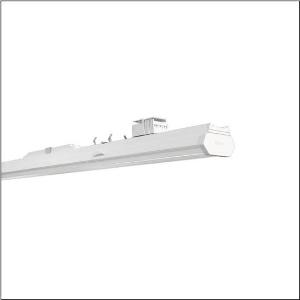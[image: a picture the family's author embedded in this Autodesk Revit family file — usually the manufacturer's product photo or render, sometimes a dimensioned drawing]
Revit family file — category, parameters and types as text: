
# Revit family: licross_r__11_protected_mo_51tp11dn495g_6ace
name_source: partatom
category: Lighting Fixtures
units: mm (PartAtom-declared; Revit-internal decimal feet)

## family parameters
Cut with Voids When Loaded = No
Host = Face
Light Source = No
Part Type = Normal
Room Calculation Point = No
Round Connector Dimension = Use Diameter
Shared = No

## types (1)
- --- (1 x LED, 9930 lm, 57.1 W, 4000K)
    Apparent Load = 57 VA
    CIE Flux Codes = 83 94 98 100 100
    Color Rendering = 80
    Color Temperature = 4000K
    Default Elevation = 1800 mm
    Description = Licross® 11 Protected MO, luminaire insert, of sheet steel, galvanised, coil coated, white, length: 1.500mm, width: 90mm, height: 101mm, LED rated luminous flux: 9.980lm, light colour: 840, SDCM (Standard Deviation of Colour Matching)MacAdam ≤ 2 SDCM (initial), control gear: DALI 2, with plug, 5-pole, with phase selection, mains connection: 220..240V, AC, 50/60Hz, rated input power: 57W, internal wiring halogen-free, primary light control with lens, of plastic, primary optical cover: cover, of PMMA, light emission: direct distribution, primary light characteristic: symmetric, protection rating (complete): IP64, insulation class (complete): insulation class I (protective earthing), certification: CE, ENEC, VDE, UKCA, protection symbol: D if used in an environment with conductive dust loads with corresponding accessories, impact resistance: IK06, permissible ambient temperature for indoor applications: -25..+35°C, corresponds to IFS (International Featured Standards) requirements for safety and quality in the food industry, reducing of maximum allowable ambient temperature of 5°C with ceiling mounting, LABS conformity tested according to VDMA 24364:2018-05, packaging unit: 1 piece
    Height = 92 mm
    Lamp = 1 x LED
    Lamp Light Flux = 9930 lm
    Lamp Power = 57.1 W
    Lamp count = 1
    Length = 1500 mm
    Luminous efficacy = 174 lm/W
    Manufacturer = Siteco
    ModVariant = No
    Model = 51TP11DN495G
    Mounting Place = Ceiling
    Mounting Type = Pendant
    Number of Poles = 1
    OnlyDefault = Yes
    Power Factor = 1
    Product Name = Licross® 11 Protected MO
    Product group = luminaire insert | ceiling pendant
    ProductGroupID = 901
    Protection Class = Protection class I
    Protection Degree = IP 64
    RLX_Detail_Level = 1
    RLX_Emergency_Light_Flux = 0 lm
    RLX_Emergency_Type = 0
    RLX_Emergency_Type_DB = No
    RlxData = <blob elided: 24237 chars, md5=f55acf6c>
    Socket = socket
    Standby Power = 0 W
    System Light Flux = 9930 lm
    System Power = 57 W
    Type Comments = factory setting: luminous flux: 100 % | dim-lin: 254 | 378 mA
    Type Image = l_1256148.jpg
    URL = http://relux.com
    VarID = @adj_106473
    Voltage = 0 V
    Weight = 0.00 kg
    Width = 88 mm

## geometry (parser evidence)
native form markers: Blend x4, Sweep x11
no freeform markers — native parametric forms only
